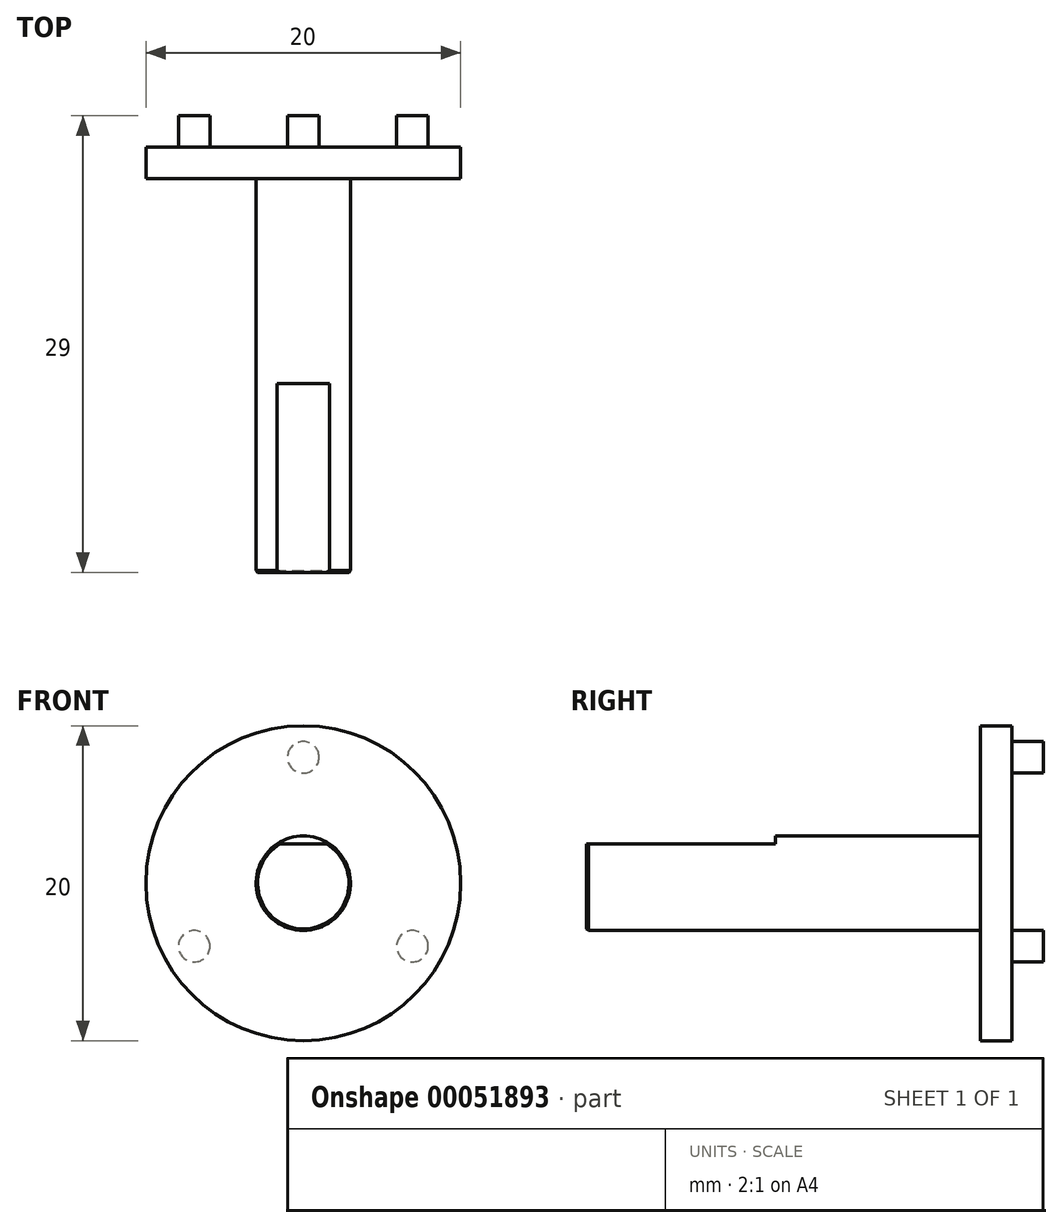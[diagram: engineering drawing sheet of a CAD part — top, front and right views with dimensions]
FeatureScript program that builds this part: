
annotation { "Feature Type Name" : "Feature", "Feature Type Description" : "" }
export const myFeature = defineFeature(function(context is Context, id is Id, definition is map)
    precondition{}
    {
        {
            var Q0;
            Q0=qCreatedBy(makeId("Front.planeOp"),FACE);
            var sketch = newSketch(context, id + "F0", { "sketchPlane" : qUnion([Q0])});
            skCircle(sketch, "E0", {"center": v(0, 0) * mm, "radius": 3 * mm});
            skSolve(sketch);
        }
        {
            var Q0;
            Q0 = qSketchRegion(id + "F0", true);
            extrude(context, id + "F1", {"entities" : qUnion([Q0]), "depth" : 25 * mm});
        }
        {
            var Q0;
            Q0=makeQuery(id+"F1.opExtrude","CAP_FACE",FACE,{"disambiguationData":[OSD([sQuery(id+"F0.wireOp",EDGE,"E0")])],"isStart":false});
            var sketch = newSketch(context, id + "F2", { "sketchPlane" : qUnion([Q0])});
            skLineSegment(sketch, "E1", {"start": v(-1.66, 2.5) * mm, "end": v(1.66, 2.5) * mm});
            skArc(sketch, "E2", {"start": v(-1.66, 2.5) * mm, "mid": v(0, 3) * mm, "end": v(1.66, 2.5) * mm});
            skSolve(sketch);
        }
        {
            var Q0;
            Q0 = qSketchRegion(id + "F2", true);
            extrude(context, id + "F3", {"entities" : qUnion([Q0]), "operationType" : NewBodyOperationType.REMOVE, "flatOperationType" : FlatOperationType.REMOVE, "oppositeDirection" : true, "offsetDistance" : 25 * mm, "depth" : 12 * mm, "domain" : OperationDomain.MODEL});
        }
        {
            var Q0;
            Q0=makeQuery(id+"F1.opExtrude","CAP_EDGE",EDGE,{"disambiguationData":[OSD([sQuery(id+"F0.wireOp",EDGE,"E0")])],"isStart":false});
            var Q1;
            {var subQ0=sQuery(id+"F2.wireOp",EDGE,"E2");var subQ1=sQuery(id+"F2.wireOp",EDGE,"E1");var subQ2=sQuery(id+"F0.wireOp",EDGE,"E0");Q1=makeQuery(id+"F3.boolean.opBoolean","COPY",EDGE,{"derivedFrom":makeQuery(id+"F3.opExtrude","SWEPT_EDGE",EDGE,{"disambiguationData":[OSD([subQ2,subQ1,subQ0]),TDD([makeQuery(id+"F2.imprint","INTERSECT",VERTEX,{"disambiguationData":[OD(1.0)],"derivedFrom":[makeQuery(id+"F1.opExtrude","CAP_EDGE",EDGE,{"disambiguationData":[OSD([subQ2])],"isStart":false}),subQ1,subQ0]})])]})});}
            var Q2;
            {var subQ0=sQuery(id+"F2.wireOp",EDGE,"E2");var subQ1=sQuery(id+"F2.wireOp",EDGE,"E1");var subQ2=sQuery(id+"F0.wireOp",EDGE,"E0");Q2=makeQuery(id+"F3.boolean.opBoolean","COPY",EDGE,{"derivedFrom":makeQuery(id+"F3.opExtrude","SWEPT_EDGE",EDGE,{"disambiguationData":[OSD([subQ2,subQ1,subQ0]),TDD([makeQuery(id+"F2.imprint","INTERSECT",VERTEX,{"disambiguationData":[OD(0.0)],"derivedFrom":[makeQuery(id+"F1.opExtrude","CAP_EDGE",EDGE,{"disambiguationData":[OSD([subQ2])],"isStart":false}),subQ1,subQ0]})])]})});}
            var Q3;
            Q3=makeQuery(id+"F3.boolean.opBoolean","COPY",EDGE,{"derivedFrom":makeQuery(id+"F3.opExtrude","CAP_EDGE",EDGE,{"disambiguationData":[OSD([sQuery(id+"F2.wireOp",EDGE,"E2")])],"isStart":false})});
            chamfer(context, id + "F4", {"entities" : qUnion([Q0, Q1, Q2, Q3]), "width" : 0.1 * mm, "tangentPropagation" : true});
        }
        {
            var Q0;
            Q0=makeQuery(id+"F1.opExtrude","CAP_FACE",FACE,{"disambiguationData":[OSD([sQuery(id+"F0.wireOp",EDGE,"E0")])],"isStart":true});
            var sketch = newSketch(context, id + "F5", { "sketchPlane" : qUnion([Q0])});
            skCircle(sketch, "E3", {"center": v(0, 0) * mm, "radius": 10 * mm});
            skSolve(sketch);
        }
        {
            var Q0;
            Q0 = qSketchRegion(id + "F5", true);
            extrude(context, id + "F6", {"entities" : qUnion([Q0]), "operationType" : NewBodyOperationType.ADD, "depth" : 2 * mm});
        }
        {
            var Q0;
            Q0=makeQuery(id+"F6.opExtrude","CAP_FACE",FACE,{"disambiguationData":[OSD([sQuery(id+"F5.wireOp",EDGE,"E3")])],"isStart":false});
            var sketch = newSketch(context, id + "F7", { "sketchPlane" : qUnion([Q0])});
            skCircle(sketch, "E4", {"center": v(0, 0) * mm, "radius": 8 * mm, "construction": true});
            skLineSegment(sketch, "E5", {"start": v(0, 0) * mm, "end": v(0, 10) * mm, "construction": true});
            skCircle(sketch, "E6", {"center": v(0, 8) * mm, "radius": 1 * mm});
            skCircle(sketch, "E7.1.0", {"center": v(-6.93, -4) * mm, "radius": 1 * mm});
            skCircle(sketch, "E7.2.0", {"center": v(6.93, -4) * mm, "radius": 1 * mm});
            skSolve(sketch);
        }
        {
            var Q0;
            Q0 = qSketchRegion(id + "F7", true);
            extrude(context, id + "F8", {"entities" : qUnion([Q0]), "operationType" : NewBodyOperationType.ADD, "depth" : 2 * mm});
        }
    });
